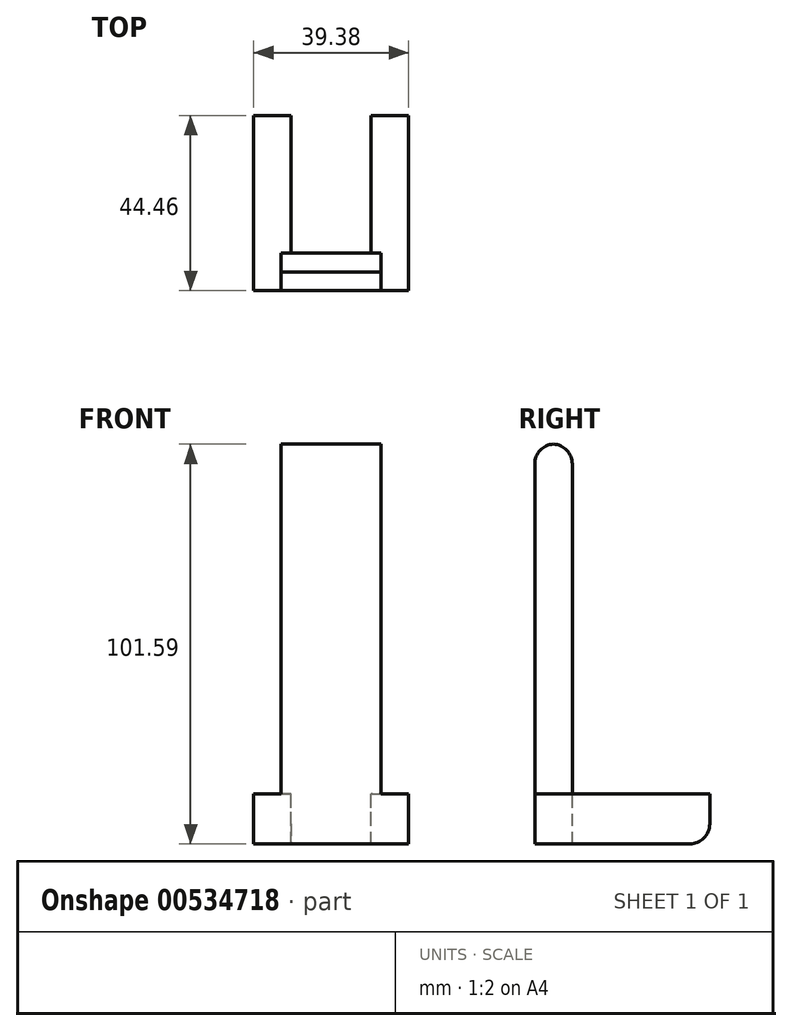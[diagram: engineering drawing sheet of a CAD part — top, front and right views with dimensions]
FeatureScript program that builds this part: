
annotation { "Feature Type Name" : "Feature", "Feature Type Description" : "" }
export const myFeature = defineFeature(function(context is Context, id is Id, definition is map)
    precondition{}
    {
        {
            var Q0;
            Q0=qCreatedBy(makeId("Top.planeOp"),FACE);
            var sketch = newSketch(context, id + "F0", { "sketchPlane" : qUnion([Q0])});
            skLineSegment(sketch, "E0.top", {"start": v(10.16, -12.7) * mm, "end": v(-10.16, -12.7) * mm});
            skLineSegment(sketch, "E0.left", {"start": v(10.16, 12.7) * mm, "end": v(10.16, -12.7) * mm});
            skLineSegment(sketch, "E0.right", {"start": v(-10.16, 12.7) * mm, "end": v(-10.16, -12.7) * mm});
            skPoint(sketch, "E0.middle", {"position": v(0, 0) * mm});
            skLineSegment(sketch, "E1.bottom", {"start": v(19.69, 22.22) * mm, "end": v(10.16, 22.22) * mm});
            skLineSegment(sketch, "E1.top", {"start": v(19.69, -22.22) * mm, "end": v(-19.69, -22.22) * mm});
            skLineSegment(sketch, "E1.left", {"start": v(19.69, 22.23) * mm, "end": v(19.69, -22.23) * mm});
            skLineSegment(sketch, "E1.right", {"start": v(-19.68, 22.23) * mm, "end": v(-19.68, -22.23) * mm});
            skLineSegment(sketch, "E2", {"start": v(-10.16, 12.7) * mm, "end": v(-10.16, 22.22) * mm});
            skLineSegment(sketch, "E3", {"start": v(10.16, 12.7) * mm, "end": v(10.16, 22.22) * mm});
            skLineSegment(sketch, "E4.trimOffspring", {"start": v(-10.16, 22.22) * mm, "end": v(-19.69, 22.22) * mm});
            skSolve(sketch);
        }
        {
            var Q0;
            Q0=makeQuery(id+"F0.imprint","IMPRINT",FACE,{"disambiguationData":[TD([[makeQuery(id+"F0.imprint","IMPRINT",EDGE,{"derivedFrom":sQuery(id+"F0.wireOp",EDGE,"E0.bottom")}),-1.0]])]});
            var Q1;
            Q1=makeQuery(id+"F0.imprint","IMPRINT",FACE,{"disambiguationData":[TD([[makeQuery(id+"F0.imprint","IMPRINT",EDGE,{"derivedFrom":sQuery(id+"F0.wireOp",EDGE,"E0.top")}),1.0]])]});
            extrude(context, id + "F1", {"entities" : qUnion([Q0, Q1]), "oppositeDirection" : true, "depth" : 12.7 * mm, "offsetDistance" : 25.4 * mm});
        }
        {
            var Q0;
            Q0=makeQuery(id+"F1.opExtrude","CAP_FACE",FACE,{"disambiguationData":[OSD([sQuery(id+"F0.wireOp",EDGE,"E0.top"),sQuery(id+"F0.wireOp",EDGE,"E0.left"),sQuery(id+"F0.wireOp",EDGE,"E0.right"),sQuery(id+"F0.wireOp",EDGE,"E1.bottom"),sQuery(id+"F0.wireOp",EDGE,"E1.top"),sQuery(id+"F0.wireOp",EDGE,"E1.left"),sQuery(id+"F0.wireOp",EDGE,"E1.right"),sQuery(id+"F0.wireOp",EDGE,"E2"),sQuery(id+"F0.wireOp",EDGE,"E3"),sQuery(id+"F0.wireOp",EDGE,"E4.trimOffspring")])],"isStart":true});
            var sketch = newSketch(context, id + "F2", { "sketchPlane" : qUnion([Q0])});
            skLineSegment(sketch, "E5.bottom", {"start": v(-12.7, -22.23) * mm, "end": v(12.7, -22.22) * mm});
            skLineSegment(sketch, "E5.top", {"start": v(-12.7, -12.7) * mm, "end": v(12.7, -12.7) * mm});
            skLineSegment(sketch, "E5.left", {"start": v(-12.7, -22.23) * mm, "end": v(-12.7, -12.7) * mm});
            skLineSegment(sketch, "E5.right", {"start": v(12.7, -22.22) * mm, "end": v(12.7, -12.7) * mm});
            skSolve(sketch);
        }
        {
            var Q0;
            Q0=makeQuery(id+"F2.imprint","IMPRINT",FACE,{"disambiguationData":[TD([[makeQuery(id+"F2.imprint","IMPRINT",EDGE,{"derivedFrom":sQuery(id+"F2.wireOp",EDGE,"E5.bottom")}),-1.0]])]});
            extrude(context, id + "F3", {"entities" : qUnion([Q0]), "operationType" : NewBodyOperationType.ADD, "depth" : 88.9 * mm, "offsetDistance" : 25.4 * mm});
        }
        {
            var Q0;
            Q0=makeQuery(id+"F3.opExtrude","CAP_EDGE",EDGE,{"disambiguationData":[OSD([sQuery(id+"F2.wireOp",EDGE,"E5.top")])],"isStart":false});
            var Q1;
            Q1=makeQuery(id+"F3.opExtrude","CAP_EDGE",EDGE,{"disambiguationData":[OSD([sQuery(id+"F2.wireOp",EDGE,"E5.bottom")])],"isStart":false});
            fillet(context, id + "F4", {"entities" : qUnion([Q0, Q1]), "radius" : 5.08 * mm, "tangentPropagation" : true, "allowEdgeOverflow" : false});
        }
        {
            var Q0;
            Q0=makeQuery(id+"F1.opExtrude","CAP_EDGE",EDGE,{"disambiguationData":[OSD([sQuery(id+"F0.wireOp",EDGE,"E1.bottom")])],"isStart":false});
            var Q1;
            Q1=makeQuery(id+"F1.opExtrude","CAP_EDGE",EDGE,{"disambiguationData":[OSD([sQuery(id+"F0.wireOp",EDGE,"E4.trimOffspring")])],"isStart":false});
            fillet(context, id + "F5", {"entities" : qUnion([Q0, Q1]), "radius" : 5.08 * mm, "tangentPropagation" : true, "allowEdgeOverflow" : false});
        }
    });
